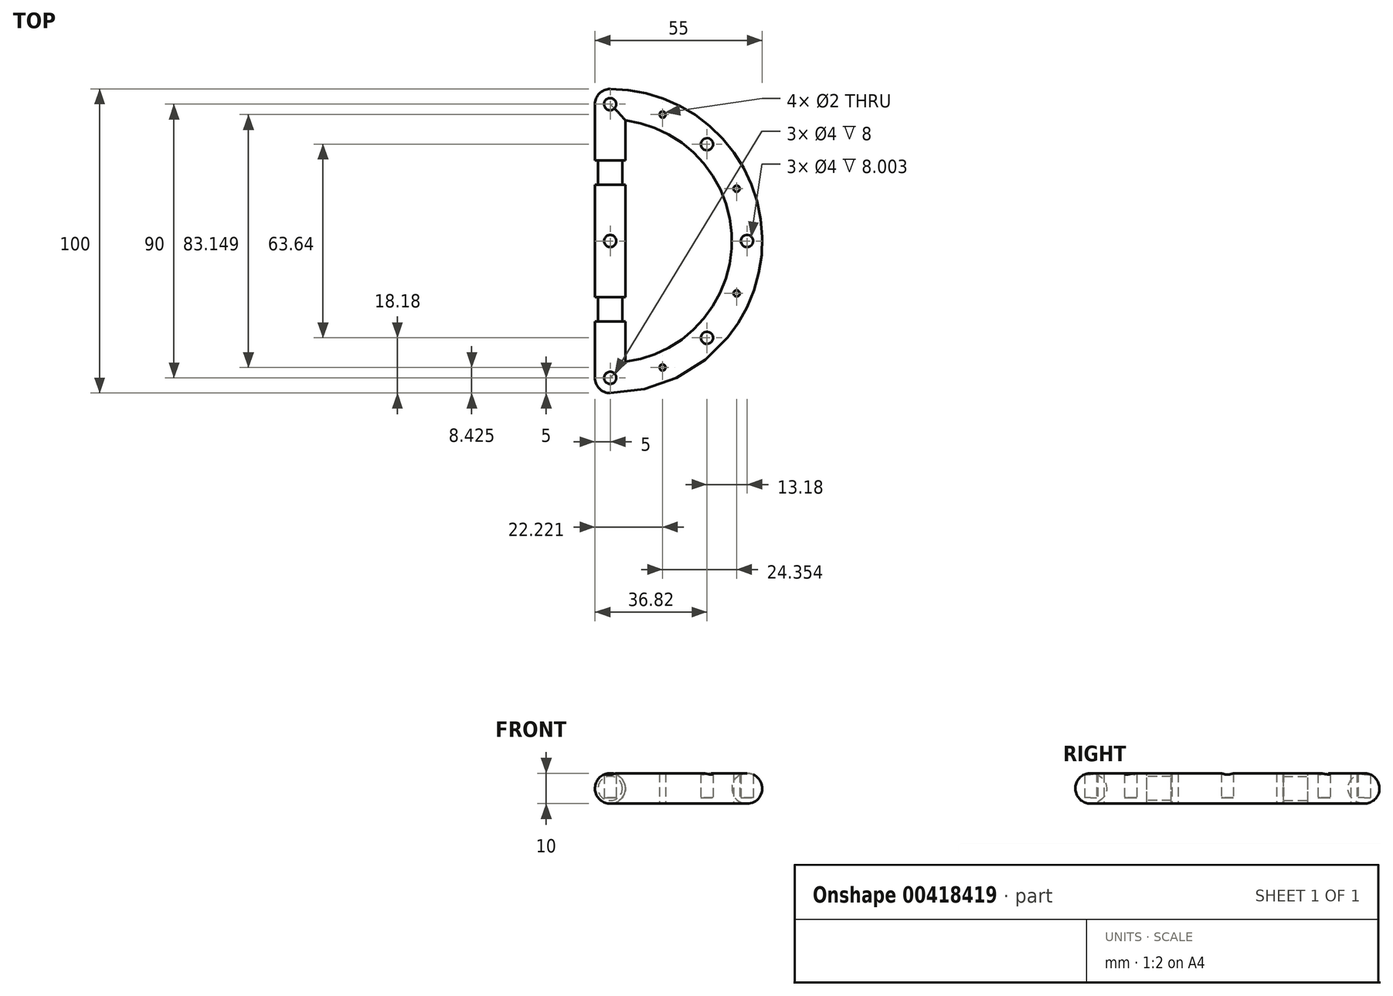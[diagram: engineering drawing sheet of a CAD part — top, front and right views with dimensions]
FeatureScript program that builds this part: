
annotation { "Feature Type Name" : "Feature", "Feature Type Description" : "" }
export const myFeature = defineFeature(function(context is Context, id is Id, definition is map)
    precondition{}
    {
        {
            var Q0;
            Q0=qCreatedBy(makeId("Front.planeOp"),FACE);
            var sketch = newSketch(context, id + "F0", { "sketchPlane" : qUnion([Q0])});
            skCircle(sketch, "E0", {"center": v(0, 0) * mm, "radius": 5 * mm});
            skLineSegment(sketch, "E1", {"start": v(0, 5) * mm, "end": v(0, -5) * mm, "construction": true});
            skSolve(sketch);
        }
        {
            var Q0;
            Q0 = qSketchRegion(id + "F0", true);
            extrude(context, id + "F1", {"entities" : qUnion([Q0]), "depth" : 90 * mm});
        }
        {
            var Q0;
            Q0=qCreatedBy(makeId("Top.planeOp"),FACE);
            var sketch = newSketch(context, id + "F2", { "sketchPlane" : qUnion([Q0])});
            skArc(sketch, "E2", {"start": v(0, 0) * mm, "mid": v(45, -45) * mm, "end": v(0, -90) * mm});
            skSolve(sketch);
        }
        {
            var Q0;
            Q0=qCreatedBy(makeId("Right.planeOp"),FACE);
            var sketch = newSketch(context, id + "F3", { "sketchPlane" : qUnion([Q0])});
            skCircle(sketch, "E3", {"center": v(-90, 0) * mm, "radius": 5 * mm});
            skSolve(sketch);
        }
        {
            var Q0;
            Q0 = qSketchRegion(id + "F3", true);
            var Q1;
            Q1=sQuery(id+"F2.wireOp",EDGE,"E2");
            sweep(context, id + "F4", {"operationType" : NewBodyOperationType.ADD, "profiles" : qUnion([Q0]), "path" : qUnion([Q1])});
        }
        {
            var Q0;
            Q0=makeQuery(id+"F1.opExtrude","CAP_FACE",FACE,{"disambiguationData":[OSD([sQuery(id+"F0.wireOp",EDGE,"E0")])],"isStart":true});
            var Q1;
            Q1=sQuery(id+"F0.wireOp",EDGE,"E0");
            var Q2;
            Q2=makeQuery(id+"F4.boolean.opBoolean","INTERSECT",EDGE,{"derivedFrom":[makeQuery(id+"F1.opExtrude","CAP_FACE",FACE,{"disambiguationData":[OSD([sQuery(id+"F0.wireOp",EDGE,"E0")])],"isStart":true}),makeQuery(id+"F4.opSweep","CAP_FACE",FACE,{"disambiguationData":[OSD([sQuery(id+"F2.wireOp",VERTEX,"E2.start"),sQuery(id+"F3.wireOp",EDGE,"E3")])],"isStart":false})]});
            revolve(context, id + "F5", {"operationType" : NewBodyOperationType.ADD, "entities" : qUnion([Q0]), "surfaceEntities" : qUnion([Q1]), "axis" : qUnion([Q2]), "revolveType" : RevolveType.FULL});
        }
        {
            var Q0;
            Q0=qCreatedBy(makeId("Front.planeOp"),FACE);
            cPlane(context, id + "F6", {"entities" : qUnion([Q0]), "cplaneType" : CPlaneType.OFFSET, "offset" : 45 * mm, "width" : 150 * mm, "height" : 150 * mm});
        }
        {
            var Q0;
            Q0=makeQuery(id+"F1.opExtrude","SWEPT_BODY",BODY,{"disambiguationData":[OSD([sQuery(id+"F0.wireOp",EDGE,"E0")])]});
            var Q1;
            Q1=qCreatedBy(id+"F6.planeOp",FACE);
            mirror(context, id + "F7", {"operationType" : NewBodyOperationType.ADD, "entities" : qUnion([Q0]), "mirrorPlane" : qUnion([Q1])});
        }
        {
            var Q0;
            Q0=qCreatedBy(makeId("Top.planeOp"),FACE);
            var sketch = newSketch(context, id + "F8", { "sketchPlane" : qUnion([Q0])});
            skCircle(sketch, "E4", {"center": v(0, 0) * mm, "radius": 2 * mm});
            skPoint(sketch, "E5.center", {"position": v(0, -45) * mm});
            skCircle(sketch, "E6.0.4.0", {"center": v(0, -90) * mm, "radius": 2 * mm});
            skCircle(sketch, "E6.0.5.0", {"center": v(31.82, -76.82) * mm, "radius": 2 * mm});
            skCircle(sketch, "E6.0.6.0", {"center": v(45, -45) * mm, "radius": 2 * mm});
            skCircle(sketch, "E6.0.7.0", {"center": v(31.82, -13.18) * mm, "radius": 2 * mm});
            skCircle(sketch, "E7.0.1.0", {"center": v(0, -45) * mm, "radius": 2 * mm});
            skCircle(sketch, "E7.1.1.0", {"center": v(0, -45) * mm, "radius": 2 * mm});
            skLineSegment(sketch, "E7.direction1", {"start": v(0, 0) * mm, "end": v(0, 0) * mm});
            skLineSegment(sketch, "E7.direction2", {"start": v(0, 0) * mm, "end": v(0, -45) * mm, "construction": true});
            skSolve(sketch);
        }
        {
            var Q0;
            Q0 = qSketchRegion(id + "F8", true);
            extrude(context, id + "F9", {"entities" : qUnion([Q0]), "operationType" : NewBodyOperationType.REMOVE, "depth" : 25 * mm, "hasSecondDirection" : true, "secondDirectionOppositeDirection" : true, "secondDirectionDepth" : 3 * mm});
        }
        {
            var Q0;
            Q0=qCreatedBy(id+"F6.planeOp",FACE);
            cPlane(context, id + "F10", {"entities" : qUnion([Q0]), "cplaneType" : CPlaneType.OFFSET, "offset" : (45 / 2) * mm, "width" : 150 * mm, "height" : 150 * mm});
        }
        {
            var Q0;
            Q0=qCreatedBy(id+"F10.planeOp",FACE);
            var sketch = newSketch(context, id + "F11", { "sketchPlane" : qUnion([Q0])});
            skCircle(sketch, "E8", {"center": v(0, 0) * mm, "radius": 5 * mm});
            skCircle(sketch, "E9", {"center": v(0, 0) * mm, "radius": 4 * mm});
            skSolve(sketch);
        }
        {
            var Q0;
            Q0 = qSketchRegion(id + "F11", true);
            extrude(context, id + "F12", {"entities" : qUnion([Q0]), "operationType" : NewBodyOperationType.REMOVE, "endBound" : BoundingType.SYMMETRIC, "oppositeDirection" : true, "depth" : 8 * mm});
        }
        {
            var Q0;
            Q0=makeQuery(id+"F1.opExtrude","SWEPT_BODY",BODY,{"disambiguationData":[OSD([sQuery(id+"F0.wireOp",EDGE,"E0")])]});
            var Q1;
            Q1=qCreatedBy(id+"F6.planeOp",FACE);
            mirror(context, id + "F13", {"operationType" : NewBodyOperationType.INTERSECT, "entities" : qUnion([Q0]), "mirrorPlane" : qUnion([Q1])});
        }
        {
            var Q0;
            Q0=qCreatedBy(makeId("Top.planeOp"),FACE);
            var sketch = newSketch(context, id + "F14", { "sketchPlane" : qUnion([Q0])});
            skCircle(sketch, "E10", {"center": v(0, 0) * mm, "radius": 1 * mm, "construction": true});
            skPoint(sketch, "E11.center", {"position": v(0, -45) * mm});
            skCircle(sketch, "E12.0.9.0", {"center": v(17.22, -86.57) * mm, "radius": 1 * mm});
            skCircle(sketch, "E12.0.11.0", {"center": v(41.57, -62.22) * mm, "radius": 1 * mm});
            skCircle(sketch, "E12.0.13.0", {"center": v(41.57, -27.78) * mm, "radius": 1 * mm});
            skCircle(sketch, "E12.0.15.0", {"center": v(17.22, -3.43) * mm, "radius": 1 * mm});
            skSolve(sketch);
        }
        {
            var Q0;
            Q0 = qSketchRegion(id + "F14", true);
            extrude(context, id + "F15", {"entities" : qUnion([Q0]), "operationType" : NewBodyOperationType.REMOVE, "endBound" : BoundingType.THROUGH_ALL, "depth" : 25 * mm, "hasSecondDirection" : true, "secondDirectionBound" : SecondDirectionBoundingType.THROUGH_ALL, "secondDirectionOppositeDirection" : true, "secondDirectionDepth" : 25 * mm});
        }
    });
